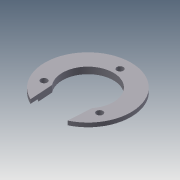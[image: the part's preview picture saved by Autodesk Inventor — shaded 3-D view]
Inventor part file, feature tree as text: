
AUTODESK INVENTOR PART (.ipt)
format: ipt  version: 2012 SP1 (Build 160190100, 190)  size: 114,176 bytes
history: native  units: in
note: dims shown in document units (in); Inventor stores cm internally (conversion verified against a paired STEP export)
features: sketch x3, extrude x2, hole x1, pattern_circular x1
ambient origin geometry x8: Origin, YZ Plane, XZ Plane, XY Plane, X Axis, Y Axis, Z Axis, Center Point
bodies: Solid1 (feature_tree)
feature tree (7):
  extrude  "Extrusion1"  Depth=0.814in
  extrude  "Extrusion2"  Depth=0.5906in
  hole  "Hole1"  [1 undecoded]
  pattern_circular  "Circular Pattern1"  [2 undecoded]
  sketch  "Sketch2"  dims[d0=1.375in d1=0.814in]
  sketch  "Sketch3"  dims[d2=0.64in d3=0.5906in]
  sketch  "Sketch4"  dims[d4=0.065in d5=0.0in d6=1.15in d7=0.0394in d8=0.0in d9=0.513in d10=0.104in d11=0.2362in d12=0.1575in d13=0.0787in d14=90.0deg d15=0.315in d16=0.8108in d17=1.1811in d18=360.0deg]
note: 3 required parameter values undecoded (feature->parameter linkage not recoverable at this tier; creation-order binding heuristic only, values carry confidence <= 0.55)
